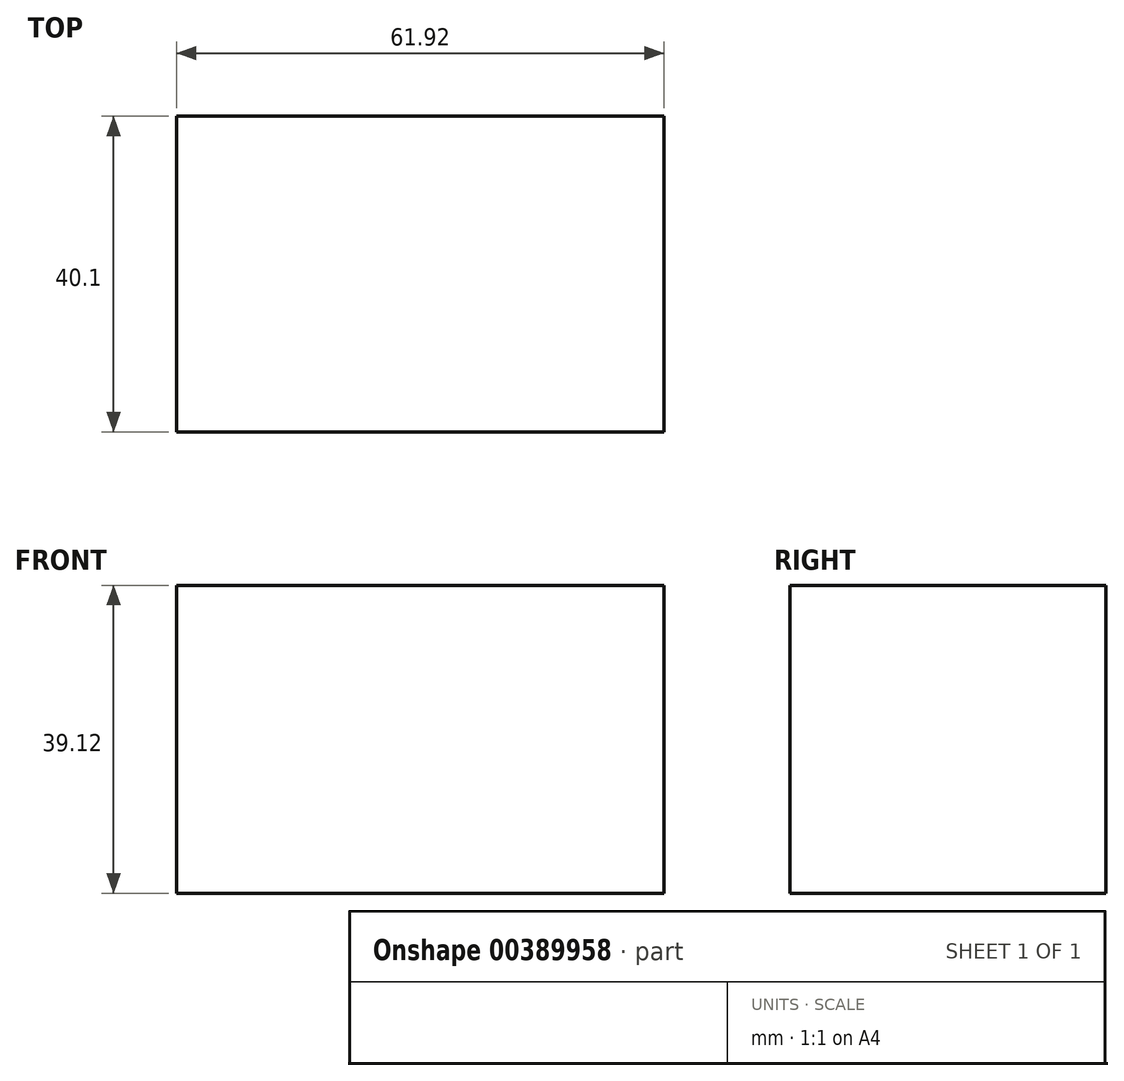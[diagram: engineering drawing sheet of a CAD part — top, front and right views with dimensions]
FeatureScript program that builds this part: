
annotation { "Feature Type Name" : "Feature", "Feature Type Description" : "" }
export const myFeature = defineFeature(function(context is Context, id is Id, definition is map)
    precondition{}
    {
        {
            var Q0;
            Q0=qCreatedBy(makeId("Top.planeOp"),FACE);
            var sketch = newSketch(context, id + "F0", { "sketchPlane" : qUnion([Q0])});
            skLineSegment(sketch, "E0.bottom", {"start": v(0, 0) * mm, "end": v(61.92, 0) * mm});
            skLineSegment(sketch, "E0.top", {"start": v(0, -40.1) * mm, "end": v(61.92, -40.1) * mm});
            skLineSegment(sketch, "E0.left", {"start": v(0, 0) * mm, "end": v(0, -40.1) * mm});
            skLineSegment(sketch, "E0.right", {"start": v(61.92, 0) * mm, "end": v(61.92, -40.1) * mm});
            skSolve(sketch);
        }
        {
            var Q0;
            Q0 = qSketchRegion(id + "F0", true);
            extrude(context, id + "F1", {"entities" : qUnion([Q0]), "depth" : 39.12 * mm});
        }
    });
